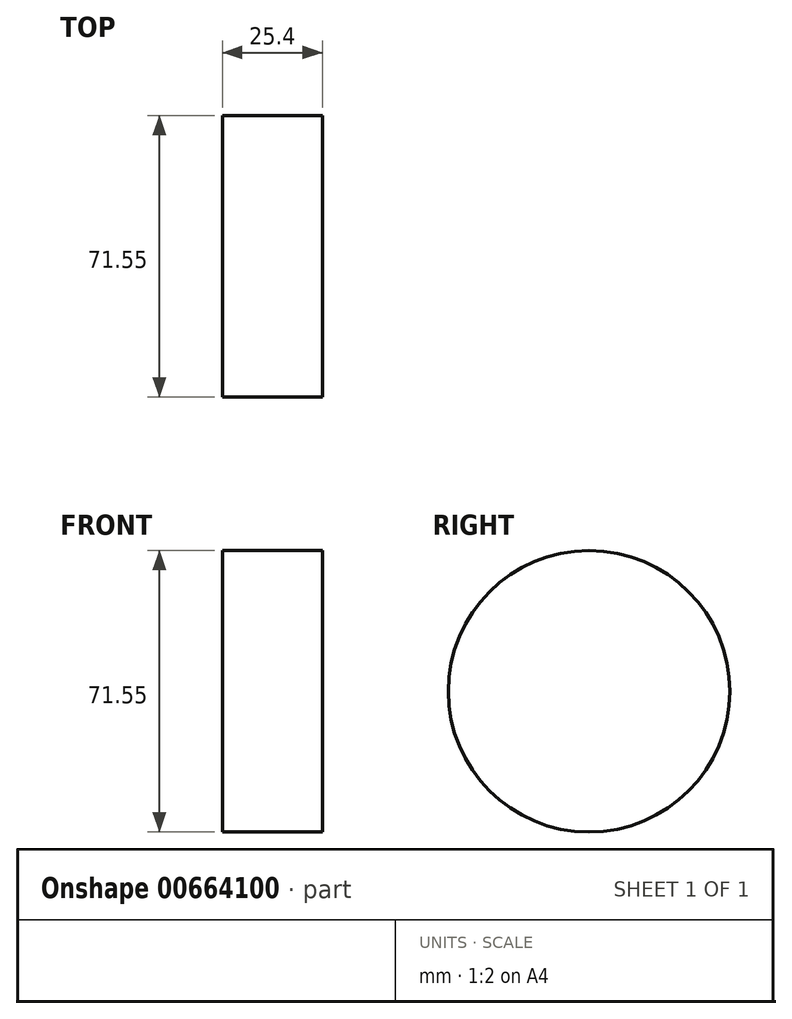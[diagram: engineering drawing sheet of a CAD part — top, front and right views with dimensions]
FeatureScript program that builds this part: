
annotation { "Feature Type Name" : "Feature", "Feature Type Description" : "" }
export const myFeature = defineFeature(function(context is Context, id is Id, definition is map)
    precondition{}
    {
        {
            var Q0;
            Q0=qCreatedBy(makeId("Right.planeOp"),FACE);
            var sketch = newSketch(context, id + "F0", { "sketchPlane" : qUnion([Q0])});
            skCircle(sketch, "E0", {"center": v(-25, 24.36) * mm, "radius": 35.77 * mm});
            skSolve(sketch);
        }
        {
            var Q0;
            Q0=makeQuery(id+"F0.imprint","IMPRINT",FACE,{"disambiguationData":[TD([[makeQuery(id+"F0.imprint","IMPRINT",EDGE,{"derivedFrom":sQuery(id+"F0.wireOp",EDGE,"E0")}),1.0]])]});
            extrude(context, id + "F1", {"entities" : qUnion([Q0]), "depth" : 25.4 * mm, "offsetDistance" : 25.4 * mm});
        }
    });
